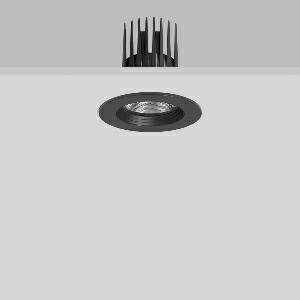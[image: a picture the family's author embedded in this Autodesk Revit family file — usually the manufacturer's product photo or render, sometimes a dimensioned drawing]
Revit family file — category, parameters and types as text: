
# Revit family: heledon_mini_e_901741_003_2_e38f
name_source: partatom
category: Lighting Fixtures
units: mm (PartAtom-declared; Revit-internal decimal feet)

## family parameters
Cut with Voids When Loaded = No
Host = Face
Light Source = No
Part Type = Normal
Room Calculation Point = No
Round Connector Dimension = Use Diameter
Shared = No

## types (1)
- HELEDON mini E (1 x LED Modul 927, 2300 lm, 2700)
    Apparent Load = 20 VA
    Approval mark = CE
    CIE Flux Codes = 99 100 100 100 100
    Color Rendering = 92
    Color Temperature = 2700
    Default Elevation = 1800 mm
    Description = Series: HELEDON mini
Round recessed downlight. Housing: die-cast aluminium, powder-coated. Black plastic ring and recessed LED to prevent glare from the side. Optical assembly with reflector made of MIRO-Silver with 98% total light reflection for outstanding efficiency - can be changed without tools. Best colour rendering index Ra>90. Suitable for Recessed ceiling mounting. Installation without tools thanks to spring fastening system. Including separate LED converter with connecting cable 600 mm.High quality converter without flickering and stroboscopic effect. Through-wiring box (5 pole) available as accessory. The following accessories can be mounted without use of tools: interchangeable lenses, decorative glasses, honeycomb louvre, clear and frosted diffusers, white interchangeable plastic ring. 
Colour: deep black, matt (RAL 9005)
Diameter: 124 mm
Height: 3 mm
Cut-out diameter: 114 mm
Recess height: 170 mm
Luminaire: recess height: 120 mm
Lamp: LED
Socket: without socket
Colour temperature: 2700K
Colour rendering index (CRI): 92
System power: 20 W
Rated luminous flux: 2300 lm
Luminous efficiency: 115 lm/W
Control gear: Regulated power supply
Protection class: II
Type of protection: IP 20
    Height = 0 mm  [stored 0 ft]
    Lamp = 1 x LED Modul 927
    Lamp Light Flux = 2300 lm
    Lamp count = 1
    Length = 124 mm  [stored 0.406824 ft]
    Lifetime = 50000 h
    Luminous efficacy = 115 lm/W
    Manufacturer = RZB
    ModVariant = No
    Model = 901741.003.2
    Mounting Place = Ceiling
    Mounting Type = Recessed
    Number of Poles = 1
    OnlyDefault = Yes
    Power Factor = 1
    Product Name = HELEDON mini E
    Product group = Recessed downlights
    ProductGroupID = 402
    Protection Class = Protection class II
    Protection Degree = IP 20
    RLX_Detail_Level = 1
    RLX_Emergency_Light_Flux = 0 lm
    RLX_Emergency_Type = 0
    RLX_Emergency_Type_DB = No
    RlxData = <blob elided: 126273 chars, md5=5eaa3f95>
    Socket = socket
    Standby Power = 0 W
    System Light Flux = 2300 lm
    System Power = 20 W
    Type Comments = Product without accessories
    Type Image = 901657.003.jpg
    URL = http://relux.com
    VarID = ---
    Voltage = 230 V
    Voltage Range = 220-240 V
    Weight = 0.00 kg
    Width = 0 mm  [stored 0 ft]

note: [stored X ft] marks values corroborated as IEEE doubles in the binary element streams (Revit-internal decimal feet)

## geometry (parser evidence)
native form markers: Blend x4, Sweep x9
no freeform markers — native parametric forms only
